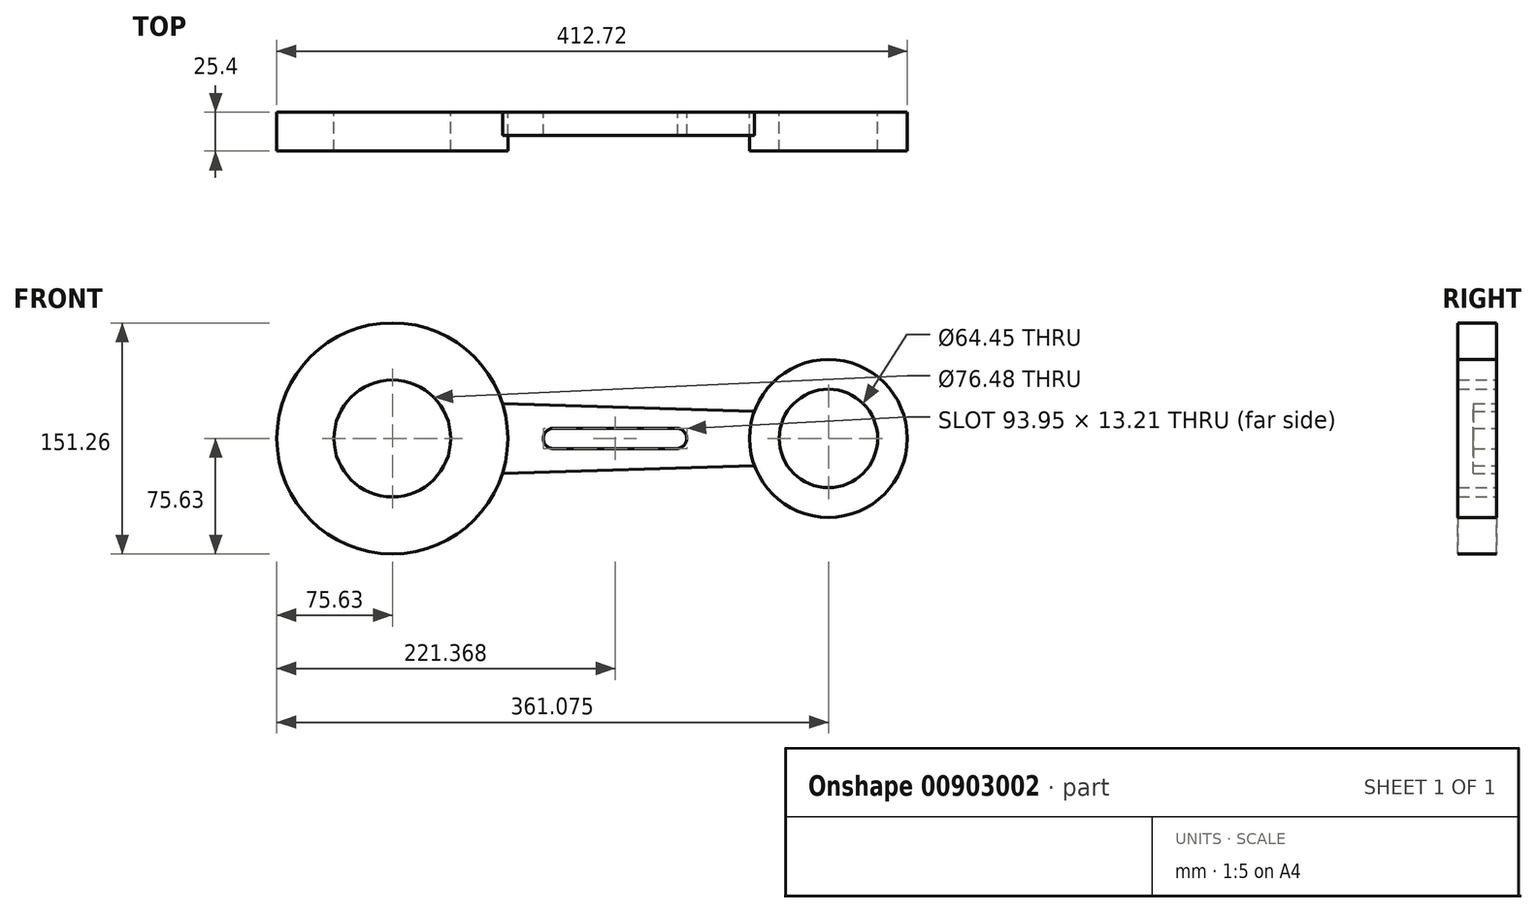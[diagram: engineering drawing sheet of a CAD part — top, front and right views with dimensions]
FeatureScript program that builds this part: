
annotation { "Feature Type Name" : "Feature", "Feature Type Description" : "" }
export const myFeature = defineFeature(function(context is Context, id is Id, definition is map)
    precondition{}
    {
        {
            var Q0;
            Q0=qCreatedBy(makeId("Front.planeOp"),FACE);
            var sketch = newSketch(context, id + "F0", { "sketchPlane" : qUnion([Q0])});
            skLineSegment(sketch, "E0.top", {"start": v(0, -74.1) * mm, "end": v(285.44, -74.1) * mm, "construction": true});
            skLineSegment(sketch, "E0.left", {"start": v(0, 0) * mm, "end": v(0, -74.1) * mm, "construction": true});
            skLineSegment(sketch, "E0.right", {"start": v(285.44, 0) * mm, "end": v(285.44, -74.1) * mm, "construction": true});
            skCircle(sketch, "E1", {"center": v(285.44, 0) * mm, "radius": 32.22 * mm});
            skCircle(sketch, "E2", {"center": v(285.44, 0) * mm, "radius": 51.65 * mm});
            skCircle(sketch, "E3", {"center": v(0, 0) * mm, "radius": 38.24 * mm});
            skLineSegment(sketch, "E4", {"start": v(72.1, 22.88) * mm, "end": v(236.95, 17.77) * mm});
            skLineSegment(sketch, "E5.MirrorCS", {"start": v(72.1, -22.88) * mm, "end": v(236.95, -17.77) * mm});
            skPoint(sketch, "E6.orphan", {"position": v(245.73, 17.5) * mm});
            skPoint(sketch, "E7.orphan", {"position": v(245.73, -17.5) * mm});
            skCircle(sketch, "E8", {"center": v(0, 0) * mm, "radius": 75.63 * mm});
            skPoint(sketch, "E9.orphan", {"position": v(62.53, 23.17) * mm});
            skPoint(sketch, "E10.orphan", {"position": v(62.53, -23.17) * mm});
            skLineSegment(sketch, "E11.bottom", {"start": v(105.36, 6.6) * mm, "end": v(186.8, 6.6) * mm});
            skLineSegment(sketch, "E12", {"start": v(0, 0) * mm, "end": v(98.76, 0) * mm, "construction": true});
            skLineSegment(sketch, "E13.MirrorCS", {"start": v(105.36, -6.6) * mm, "end": v(186.8, -6.6) * mm});
            skArc(sketch, "E14", {"start": v(186.8, -6.6) * mm, "mid": v(192.71, 0) * mm, "end": v(186.8, 6.6) * mm});
            skPoint(sketch, "E14.third.point", {"position": v(192.71, 0) * mm});
            skArc(sketch, "E15", {"start": v(105.36, 6.6) * mm, "mid": v(98.76, 0) * mm, "end": v(105.36, -6.6) * mm});
            skPoint(sketch, "E15.third.point", {"position": v(111.1, -3.28) * mm});
            skLineSegment(sketch, "E16.trimOffspring", {"start": v(192.71, 0) * mm, "end": v(285.44, 0) * mm, "construction": true});
            skSolve(sketch);
        }
        {
            var Q0;
            Q0=makeQuery(id+"F0.imprint","IMPRINT",FACE,{"disambiguationData":[TD([[makeQuery(id+"F0.imprint","IMPRINT",EDGE,{"derivedFrom":sQuery(id+"F0.wireOp",EDGE,"E3")}),-1.0]])]});
            var Q1;
            Q1=makeQuery(id+"F0.imprint","IMPRINT",FACE,{"disambiguationData":[TD([[makeQuery(id+"F0.imprint","IMPRINT",EDGE,{"derivedFrom":sQuery(id+"F0.wireOp",EDGE,"E1")}),-1.0]])]});
            extrude(context, id + "F1", {"entities" : qUnion([Q0, Q1]), "depth" : 25.4 * mm, "offsetDistance" : 25.4 * mm});
        }
        {
            var Q0;
            {var subQ0=sQuery(id+"F0.wireOp",EDGE,"E4");Q0=makeQuery(id+"F0.imprint","IMPRINT",FACE,{"disambiguationData":[TD([[makeQuery(id+"F0.imprint","IMPRINT",EDGE,{"derivedFrom":subQ0}),-1.0]])]});}
            extrude(context, id + "F2", {"entities" : qUnion([Q0]), "depth" : 15.24 * mm, "offsetDistance" : 25.4 * mm});
        }
    });
